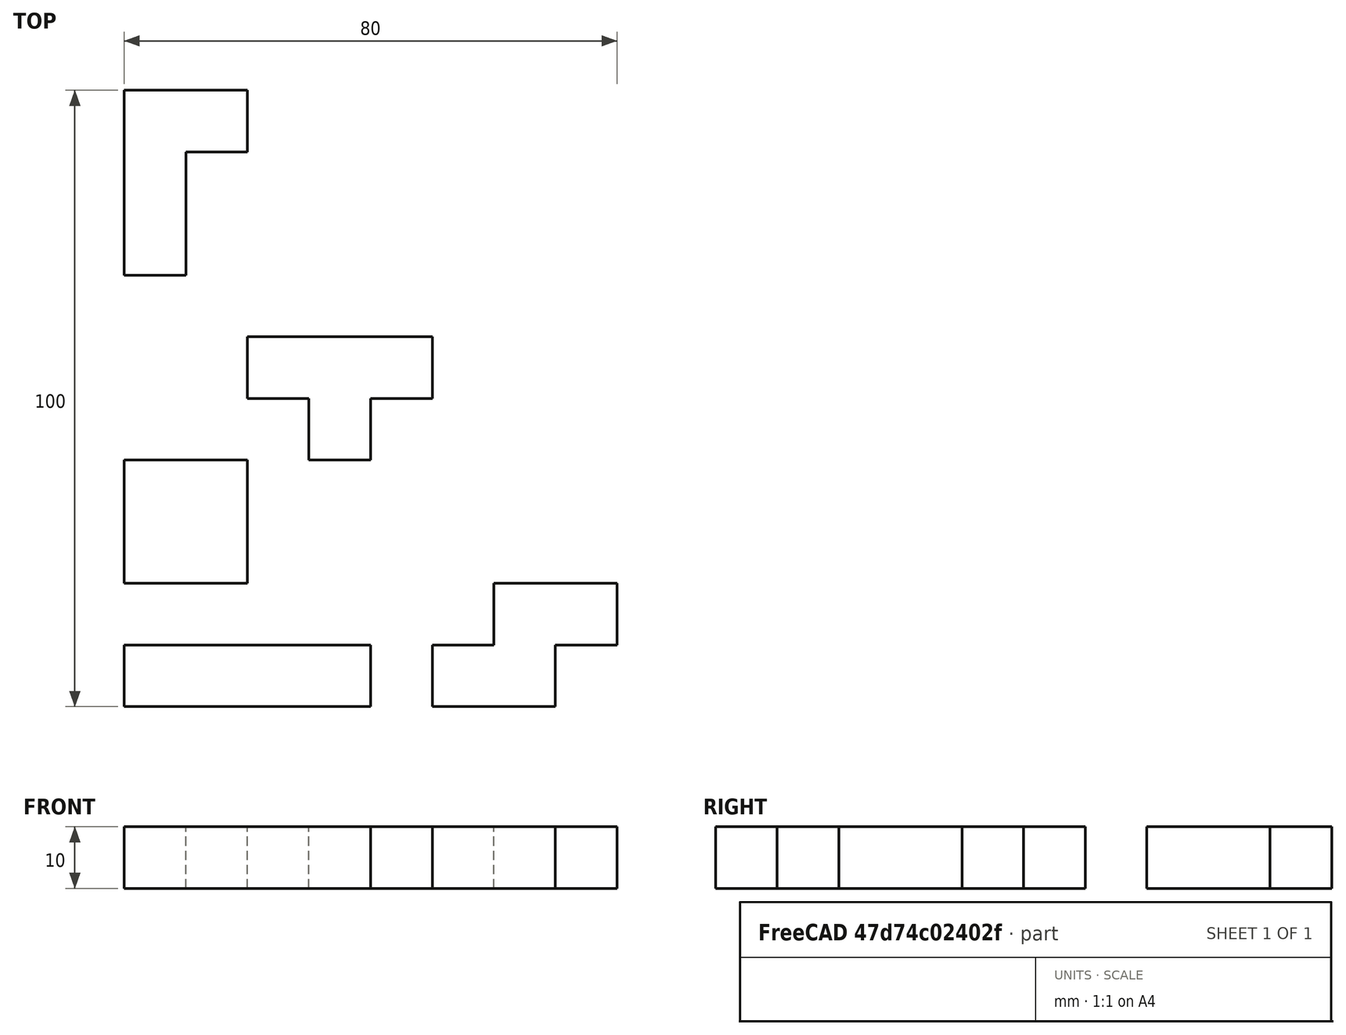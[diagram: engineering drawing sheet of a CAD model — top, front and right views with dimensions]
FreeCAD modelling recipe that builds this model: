
FCSTD DOCUMENT  (FreeCAD 0.21R33694 (Git))
Label: OJT1_T05R03_tetris
License: All rights reserved
LicenseURL: http://en.wikipedia.org/wiki/All_rights_reserved
objects: Part::Box×20, Part::MultiFuse×5
note: 25 computed .brp shape members not serialized (recipe doc carries the construction recipe); baked Part::Feature solids carry a one-line shape summary decoded from their .brp

FEATURE [Part::Box] Box  label="Cube"
  AttacherType = Attacher::AttachEngine3D
  Height = 10
  Length = 10
  Width = 10
FEATURE [Part::Box] Box001  label="Cube001"
  AttacherType = Attacher::AttachEngine3D
  Height = 10
  Length = 10
  Placement = pos=(10,0,0) rot=(0,0,1;0rad)
  Width = 10
FEATURE [Part::Box] Box002  label="Cube002"
  AttacherType = Attacher::AttachEngine3D
  Height = 10
  Length = 10
  Placement = pos=(20,0,0) rot=(0,0,1;0rad)
  Width = 10
FEATURE [Part::Box] Box003  label="Cube003"
  AttacherType = Attacher::AttachEngine3D
  Height = 10
  Length = 10
  Placement = pos=(30,0,0) rot=(0,0,1;0rad)
  Width = 10
FEATURE [Part::Box] Box004  label="Cube004"
  AttacherType = Attacher::AttachEngine3D
  Height = 10
  Length = 10
  Placement = pos=(0,20,0) rot=(0,0,1;0rad)
  Width = 10
FEATURE [Part::MultiFuse] Fusion
  Refine = true
  Shapes = -> [Box,Box001,Box002,Box003]
FEATURE [Part::Box] Box005  label="Cube005"
  AttacherType = Attacher::AttachEngine3D
  Height = 10
  Length = 10
  Placement = pos=(10,20,0) rot=(0,0,1;0rad)
  Width = 10
FEATURE [Part::Box] Box006  label="Cube006"
  AttacherType = Attacher::AttachEngine3D
  Height = 10
  Length = 10
  Placement = pos=(0,30,0) rot=(0,0,1;0rad)
  Width = 10
FEATURE [Part::Box] Box007  label="Cube007"
  AttacherType = Attacher::AttachEngine3D
  Height = 10
  Length = 10
  Placement = pos=(10,30,0) rot=(0,0,1;0rad)
  Width = 10
FEATURE [Part::MultiFuse] Fusion001
  Refine = true
  Shapes = -> [Box004,Box005,Box006,Box007]
FEATURE [Part::Box] Box008  label="Cube008"
  AttacherType = Attacher::AttachEngine3D
  Height = 10
  Length = 10
  Placement = pos=(50,0,0) rot=(0,0,1;0rad)
  Width = 10
FEATURE [Part::Box] Box009  label="Cube009"
  AttacherType = Attacher::AttachEngine3D
  Height = 10
  Length = 10
  Placement = pos=(60,0,0) rot=(0,0,1;0rad)
  Width = 10
FEATURE [Part::Box] Box010  label="Cube010"
  AttacherType = Attacher::AttachEngine3D
  Height = 10
  Length = 10
  Placement = pos=(60,10,0) rot=(0,0,1;0rad)
  Width = 10
FEATURE [Part::Box] Box011  label="Cube011"
  AttacherType = Attacher::AttachEngine3D
  Height = 10
  Length = 10
  Placement = pos=(70,10,0) rot=(0,0,1;0rad)
  Width = 10
FEATURE [Part::MultiFuse] Fusion002
  Refine = true
  Shapes = -> [Box008,Box009,Box010,Box011]
FEATURE [Part::Box] Box012  label="Cube012"
  AttacherType = Attacher::AttachEngine3D
  Height = 10
  Length = 10
  Placement = pos=(30,40,0) rot=(0,0,1;0rad)
  Width = 10
FEATURE [Part::Box] Box013  label="Cube013"
  AttacherType = Attacher::AttachEngine3D
  Height = 10
  Length = 10
  Placement = pos=(40,50,0) rot=(0,0,1;0rad)
  Width = 10
FEATURE [Part::Box] Box014  label="Cube014"
  AttacherType = Attacher::AttachEngine3D
  Height = 10
  Length = 10
  Placement = pos=(30,50,0) rot=(0,0,1;0rad)
  Width = 10
FEATURE [Part::Box] Box015  label="Cube015"
  AttacherType = Attacher::AttachEngine3D
  Height = 10
  Length = 10
  Placement = pos=(20,50,0) rot=(0,0,1;0rad)
  Width = 10
FEATURE [Part::MultiFuse] Fusion003
  Refine = true
  Shapes = -> [Box012,Box013,Box014,Box015]
FEATURE [Part::Box] Box016  label="Cube016"
  AttacherType = Attacher::AttachEngine3D
  Height = 10
  Length = 10
  Placement = pos=(0,70,0) rot=(0,0,1;0rad)
  Width = 10
FEATURE [Part::Box] Box017  label="Cube017"
  AttacherType = Attacher::AttachEngine3D
  Height = 10
  Length = 10
  Placement = pos=(0,80,0) rot=(0,0,1;0rad)
  Width = 10
FEATURE [Part::Box] Box018  label="Cube018"
  AttacherType = Attacher::AttachEngine3D
  Height = 10
  Length = 10
  Placement = pos=(0,90,0) rot=(0,0,1;0rad)
  Width = 10
FEATURE [Part::Box] Box019  label="Cube019"
  AttacherType = Attacher::AttachEngine3D
  Height = 10
  Length = 10
  Placement = pos=(10,90,0) rot=(0,0,1;0rad)
  Width = 10
FEATURE [Part::MultiFuse] Fusion004
  Refine = true
  Shapes = -> [Box016,Box017,Box018,Box019]
